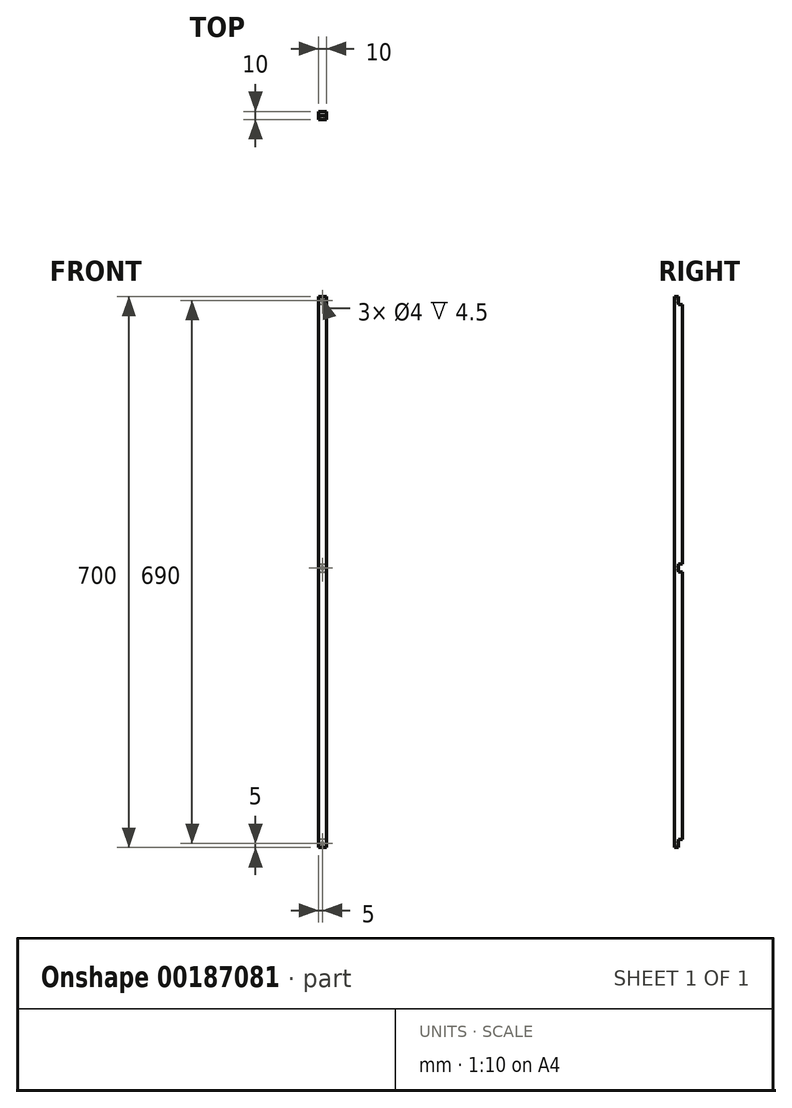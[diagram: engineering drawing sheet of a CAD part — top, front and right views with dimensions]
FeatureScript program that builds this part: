
annotation { "Feature Type Name" : "Feature", "Feature Type Description" : "" }
export const myFeature = defineFeature(function(context is Context, id is Id, definition is map)
    precondition{}
    {
        {
            var Q0;
            Q0=qCreatedBy(makeId("Right.planeOp"),FACE);
            var sketch = newSketch(context, id + "F0", { "sketchPlane" : qUnion([Q0])});
            skLineSegment(sketch, "E0", {"start": v(0, 0) * mm, "end": v(0, 340) * mm});
            skLineSegment(sketch, "E1", {"start": v(0, 340) * mm, "end": v(-5, 340) * mm});
            skLineSegment(sketch, "E2", {"start": v(-5, 340) * mm, "end": v(-5, 350) * mm});
            skLineSegment(sketch, "E3", {"start": v(-5, 350) * mm, "end": v(-10, 350) * mm});
            skLineSegment(sketch, "E4", {"start": v(-10, 350) * mm, "end": v(-10, 0) * mm});
            skLineSegment(sketch, "E5", {"start": v(-10, 0) * mm, "end": v(0, 0) * mm});
            skSolve(sketch);
        }
        {
            var Q0;
            Q0=qSketchRegion(id+"F0",true);
            extrude(context, id + "F1", {"entities" : qUnion([Q0]), "depth" : 10 * mm});
        }
        {
            var Q0;
            Q0=makeQuery(id+"F1.opExtrude","SWEPT_FACE",FACE,{"disambiguationData":[OSD([sQuery(id+"F0.wireOp",EDGE,"E2")])]});
            var sketch = newSketch(context, id + "F2", { "sketchPlane" : qUnion([Q0])});
            skCircle(sketch, "E6", {"center": v(-5, 345) * mm, "radius": 2 * mm});
            skPoint(sketch, "E6.centerSnap0", {"position": v(-5, 350) * mm});
            skPoint(sketch, "E6.centerSnap1", {"position": v(0, 345) * mm});
            skSolve(sketch);
        }
        {
            var Q0;
            Q0=qSketchRegion(id+"F2",true);
            extrude(context, id + "F3", {"entities" : qUnion([Q0]), "operationType" : NewBodyOperationType.REMOVE, "oppositeDirection" : true, "depth" : 4.5 * mm});
        }
        {
            var Q0;
            Q0=makeQuery(id+"F1.opExtrude","SWEPT_BODY",BODY,{"disambiguationData":[OSD([sQuery(id+"F0.wireOp",EDGE,"E0"),sQuery(id+"F0.wireOp",EDGE,"E1"),sQuery(id+"F0.wireOp",EDGE,"E2"),sQuery(id+"F0.wireOp",EDGE,"E3"),sQuery(id+"F0.wireOp",EDGE,"E4"),sQuery(id+"F0.wireOp",EDGE,"E5")])]});
            var Q1;
            Q1=qCreatedBy(makeId("Top.planeOp"),FACE);
            mirror(context, id + "F4", {"operationType" : NewBodyOperationType.ADD, "entities" : qUnion([Q0]), "mirrorPlane" : qUnion([Q1])});
        }
        {
            var Q0;
            {var subQ0=makeQuery(id+"F1.opExtrude","CAP_FACE",FACE,{"disambiguationData":[OSD([sQuery(id+"F0.wireOp",EDGE,"E0"),sQuery(id+"F0.wireOp",EDGE,"E1"),sQuery(id+"F0.wireOp",EDGE,"E2"),sQuery(id+"F0.wireOp",EDGE,"E3"),sQuery(id+"F0.wireOp",EDGE,"E4"),sQuery(id+"F0.wireOp",EDGE,"E5")])],"isStart":false});Q0=makeQuery(id+"F4.boolean.opBoolean","MERGE",FACE,{"derivedFrom":[subQ0,makeQuery(id+"F4.opPattern","COPY",FACE,{"derivedFrom":subQ0,"instanceName":"1"})]});}
            var sketch = newSketch(context, id + "F5", { "sketchPlane" : qUnion([Q0])});
            skLineSegment(sketch, "E7.bottom", {"start": v(0, 0) * mm, "end": v(-5, 0) * mm});
            skLineSegment(sketch, "E7.top", {"start": v(0, 10) * mm, "end": v(-5, 10) * mm});
            skLineSegment(sketch, "E7.left", {"start": v(0, 0) * mm, "end": v(0, 10) * mm});
            skLineSegment(sketch, "E7.right", {"start": v(-5, 0) * mm, "end": v(-5, 10) * mm});
            skSolve(sketch);
        }
        {
            var Q0;
            Q0 = qSketchRegion(id + "F5", true);
            extrude(context, id + "F6", {"entities" : qUnion([Q0]), "operationType" : NewBodyOperationType.REMOVE, "endBound" : BoundingType.THROUGH_ALL, "oppositeDirection" : true, "depth" : 25 * mm});
        }
        {
            var Q0;
            Q0=makeQuery(id+"F6.boolean.opBoolean","COPY",FACE,{"derivedFrom":makeQuery(id+"F6.opExtrude","SWEPT_FACE",FACE,{"disambiguationData":[OSD([sQuery(id+"F5.wireOp",EDGE,"E7.right")])]})});
            var sketch = newSketch(context, id + "F7", { "sketchPlane" : qUnion([Q0])});
            skCircle(sketch, "E8", {"center": v(-5, 5) * mm, "radius": 2 * mm});
            skPoint(sketch, "E8.centerSnap0", {"position": v(-5, 0) * mm});
            skPoint(sketch, "E8.centerSnap1", {"position": v(-10, 5) * mm});
            skSolve(sketch);
        }
        {
            var Q0;
            Q0 = qSketchRegion(id + "F7", true);
            extrude(context, id + "F8", {"entities" : qUnion([Q0]), "operationType" : NewBodyOperationType.REMOVE, "oppositeDirection" : true, "depth" : 4.5 * mm});
        }
    });
